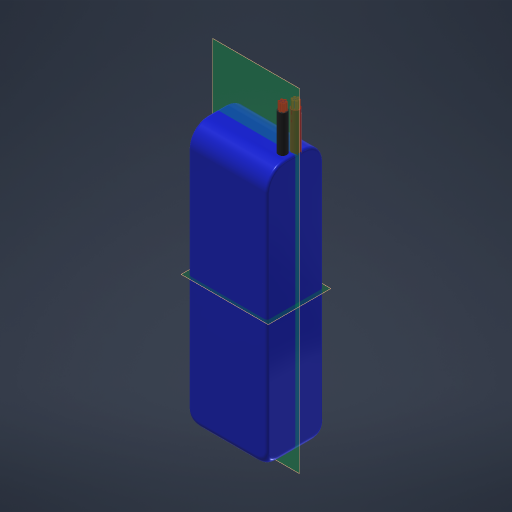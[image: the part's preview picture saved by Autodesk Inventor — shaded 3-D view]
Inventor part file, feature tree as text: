
AUTODESK INVENTOR PART (.ipt)
format: ipt  version: 2024.3 (Build 283343000, 343)  size: 439,296 bytes
history: native  units: mm
features: other x5, extrude x3, sketch x3, fillet x2
ambient origin geometry x8: Origin, YZ Plane, XZ Plane, XY Plane, X Axis, Y Axis, Z Axis, Center Point
bodies: Body1 (feature_tree)
feature tree (13):
  other  "솔리드1"
  extrude  "돌출1"  Depth=32.0mm
  fillet  "모깎기1"  Radius=105.0mm
  extrude  "돌출2"  Depth=23.0mm TaperAngle=0.0deg
  extrude  "돌출3"  Depth=8.0mm
  other  "전사1"
  fillet  "모깎기2"  Radius=3.5mm
  other  "작업 평면1"
  other  "작업 평면2"
  sketch  "스케치2"
  sketch  "스케치3"
  sketch  "스케치4"
  other  "이미지2"
